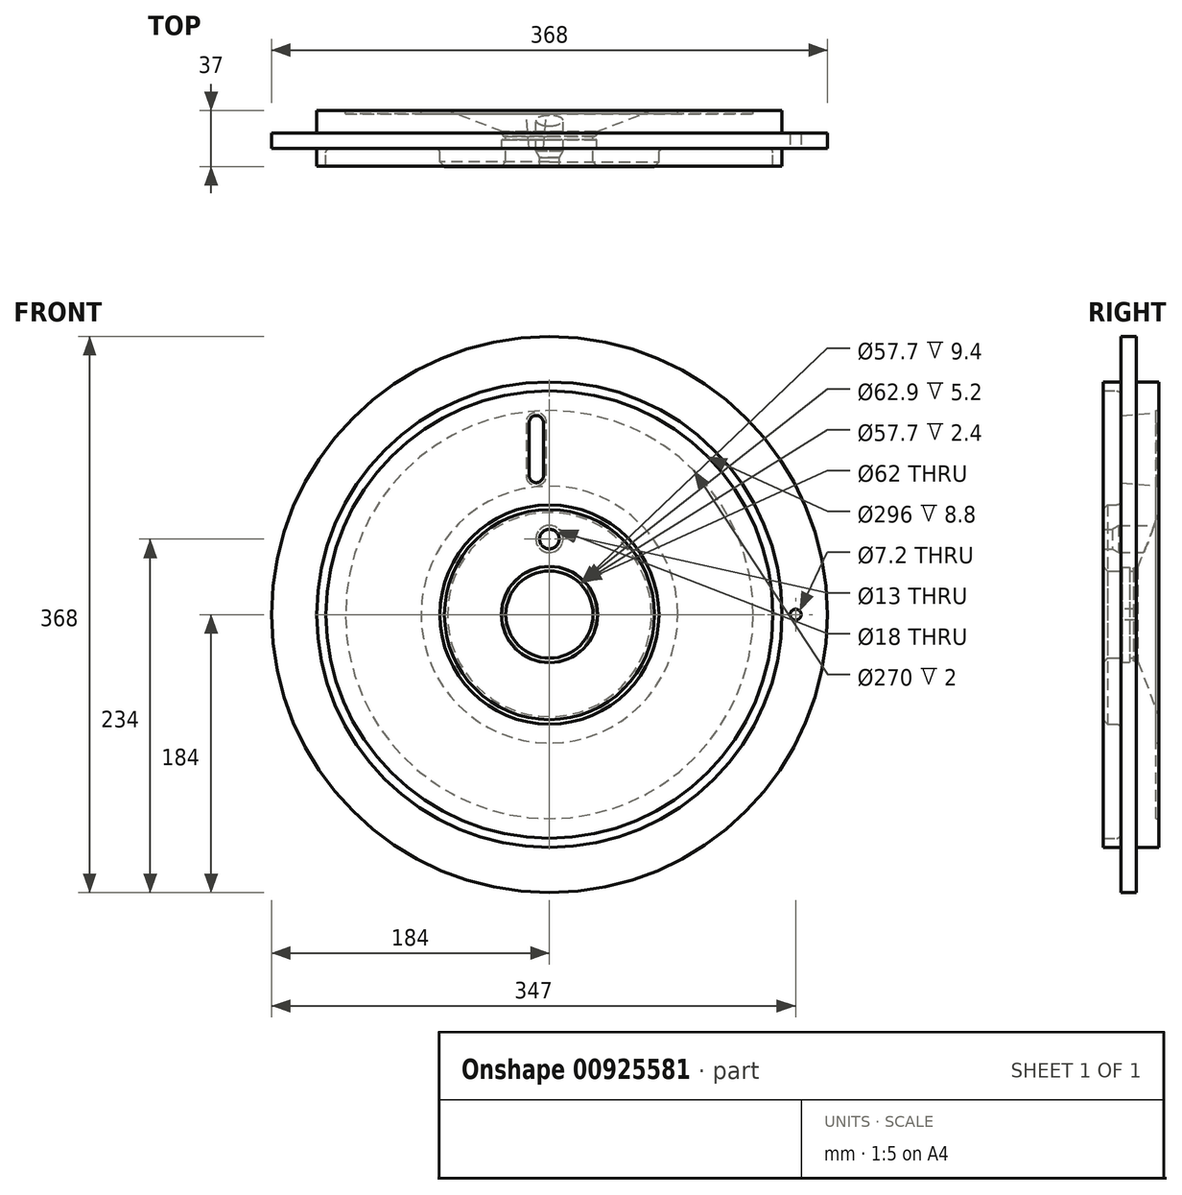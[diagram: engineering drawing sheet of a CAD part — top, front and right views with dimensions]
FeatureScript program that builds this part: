
annotation { "Feature Type Name" : "Feature", "Feature Type Description" : "" }
export const myFeature = defineFeature(function(context is Context, id is Id, definition is map)
    precondition{}
    {
        {
            var Q0;
            Q0=qCreatedBy(makeId("Top.planeOp"),FACE);
            var sketch = newSketch(context, id + "F0", { "sketchPlane" : qUnion([Q0])});
            skLineSegment(sketch, "E0", {"start": v(-72.5, 9) * mm, "end": v(-72.5, 0) * mm});
            skLineSegment(sketch, "E1", {"start": v(-72.5, 0) * mm, "end": v(-28.85, 0) * mm});
            skLineSegment(sketch, "E2", {"start": v(0, 47.35) * mm, "end": v(0, -31.33) * mm, "construction": true});
            skPoint(sketch, "E3.visualSharp", {"position": v(-72.5, 10) * mm});
            skLineSegment(sketch, "E4", {"start": v(-22.07, -0.9) * mm, "end": v(27.18, -0.9) * mm, "construction": true});
            skLineSegment(sketch, "E5", {"start": v(-154, 12) * mm, "end": v(-154, 0.2) * mm});
            skLineSegment(sketch, "E6", {"start": v(-154, 0.2) * mm, "end": v(-148, 0.2) * mm});
            skLineSegment(sketch, "E7", {"start": v(-148, 0.2) * mm, "end": v(-148, 9) * mm});
            skLineSegment(sketch, "E8", {"start": v(-28.85, 20) * mm, "end": v(-30, 20) * mm});
            skPoint(sketch, "E9.visualSharp", {"position": v(-35.7, 20) * mm});
            skLineSegment(sketch, "E10", {"start": v(-28.85, 20) * mm, "end": v(-28.85, 17.6) * mm});
            skLineSegment(sketch, "E11", {"start": v(-28.85, 17.6) * mm, "end": v(-31.45, 17.6) * mm});
            skLineSegment(sketch, "E12", {"start": v(-31.45, 17.6) * mm, "end": v(-31.45, 12.4) * mm});
            skLineSegment(sketch, "E13", {"start": v(-31.45, 12.4) * mm, "end": v(-28.85, 12.4) * mm});
            skLineSegment(sketch, "E14", {"start": v(-28.85, 12.4) * mm, "end": v(-28.85, 0) * mm});
            skLineSegment(sketch, "E15", {"start": v(-154, 12) * mm, "end": v(-184, 12) * mm});
            skLineSegment(sketch, "E16", {"start": v(-154, 37) * mm, "end": v(-67.5, 37) * mm});
            skPoint(sketch, "E17.visualSharp", {"position": v(-35, 23.4) * mm});
            skLineSegment(sketch, "E18", {"start": v(-145, 12) * mm, "end": v(-75.5, 12) * mm});
            skPoint(sketch, "E19.orphan", {"position": v(-148, 11.2) * mm});
            skPoint(sketch, "E20.visualSharp", {"position": v(-148, 12) * mm});
            skArc(sketch, "E20.filletArc", {"start": v(-145, 12) * mm, "mid": v(-147.12, 11.12) * mm, "end": v(-148, 9) * mm});
            skPoint(sketch, "E21.visualSharp", {"position": v(-72.5, 12) * mm});
            skArc(sketch, "E21.filletArc", {"start": v(-72.5, 9) * mm, "mid": v(-73.38, 11.12) * mm, "end": v(-75.5, 12) * mm});
            skLineSegment(sketch, "E22", {"start": v(-184, 12) * mm, "end": v(-184, 22) * mm});
            skLineSegment(sketch, "E23", {"start": v(-184, 22) * mm, "end": v(-154, 22) * mm});
            skLineSegment(sketch, "E24", {"start": v(-154, 22) * mm, "end": v(-154, 37) * mm});
            skLineSegment(sketch, "E25", {"start": v(-31, 23) * mm, "end": v(-67.5, 37) * mm});
            skLineSegment(sketch, "E26", {"start": v(-31, 23) * mm, "end": v(-31, 21) * mm});
            skPoint(sketch, "E27.visualSharp", {"position": v(-31, 20) * mm});
            skArc(sketch, "E27.filletArc", {"start": v(-31, 21) * mm, "mid": v(-30.7, 20.3) * mm, "end": v(-30, 20) * mm});
            skSolve(sketch);
        }
        {
            var Q0;
            Q0=makeQuery(id+"F0.imprint","IMPRINT",FACE,{"disambiguationData":[TD([[makeQuery(id+"F0.imprint","IMPRINT",EDGE,{"derivedFrom":sQuery(id+"F0.wireOp",EDGE,"E0")}),1.0]])]});
            var Q1;
            Q1=sQuery(id+"F0.wireOp",EDGE,"E2");
            revolve(context, id + "F1", {"surfaceOperationType" : NewSurfaceOperationType.NEW, "entities" : qUnion([Q0]), "axis" : qUnion([Q1]), "revolveType" : RevolveType.FULL});
        }
        {
            var Q0;
            Q0=qCreatedBy(makeId("Front.planeOp"),FACE);
            cPlane(context, id + "F2", {"entities" : qUnion([Q0]), "cplaneType" : CPlaneType.OFFSET, "offset" : 38 * mm, "oppositeDirection" : true, "width" : 150 * mm, "height" : 150 * mm});
        }
        {
            var Q0;
            Q0=qCreatedBy(makeId("Front.planeOp"),FACE);
            var sketch = newSketch(context, id + "F3", { "sketchPlane" : qUnion([Q0])});
            skCircle(sketch, "E28", {"center": v(163, 0) * mm, "radius": 3.6 * mm});
            skSolve(sketch);
        }
        {
            var Q0;
            Q0=qSketchRegion(id+"F3",true);
            extrude(context, id + "F4", {"entities" : qUnion([Q0]), "operationType" : NewBodyOperationType.REMOVE, "oppositeDirection" : true, "depth" : 50 * mm, "offsetDistance" : 25 * mm});
        }
        {
            var Q0;
            Q0=qCreatedBy(makeId("Right.planeOp"),FACE);
            var sketch = newSketch(context, id + "F5", { "sketchPlane" : qUnion([Q0])});
            skLineSegment(sketch, "E29", {"start": v(0, 50) * mm, "end": v(51.06, 50) * mm});
            skLineSegment(sketch, "E30", {"start": v(0, 56.5) * mm, "end": v(6, 56.5) * mm});
            skLineSegment(sketch, "E31", {"start": v(6, 56.5) * mm, "end": v(10.33, 59) * mm});
            skLineSegment(sketch, "E32", {"start": v(10.33, 59) * mm, "end": v(51.06, 59) * mm});
            skLineSegment(sketch, "E33", {"start": v(51.06, 59) * mm, "end": v(51.06, 50) * mm});
            skLineSegment(sketch, "E34", {"start": v(0, 50) * mm, "end": v(0, 56.5) * mm});
            skSolve(sketch);
        }
        {
            var Q0;
            Q0=qSketchRegion(id+"F5",true);
            var Q1;
            Q1=sQuery(id+"F5.wireOp",EDGE,"E29");
            revolve(context, id + "F6", {"operationType" : NewBodyOperationType.REMOVE, "surfaceOperationType" : NewSurfaceOperationType.NEW, "entities" : qUnion([Q0]), "axis" : qUnion([Q1]), "revolveType" : RevolveType.FULL, "oppositeDirection" : true});
        }
        {
            var Q0;
            Q0=makeQuery(id+"F1.opRevolve","SWEPT_EDGE",EDGE,{"disambiguationData":[OSD([sQuery(id+"F0.wireOp",EDGE,"GnCOIqdh-ukie-yiku-SOtR-T2upxGWuMmtm"),sQuery(id+"F0.wireOp",EDGE,"E1")])]});
            chamfer(context, id + "F7", {"entities" : qUnion([Q0]), "width" : 3 * mm, "tangentPropagation" : true});
        }
        {
            var Q0;
            Q0=qCreatedBy(id+"F2.planeOp",FACE);
            var sketch = newSketch(context, id + "F8", { "sketchPlane" : qUnion([Q0])});
            skCircle(sketch, "E35", {"center": v(0, 0) * mm, "radius": 85 * mm});
            skCircle(sketch, "E36", {"center": v(0, 0) * mm, "radius": 135 * mm});
            skSolve(sketch);
        }
        {
            var Q0;
            Q0=qSketchRegion(id+"F8",true);
            var Q1;
            Q1=makeQuery(id+"F1.opRevolve","SWEPT_FACE",FACE,{"disambiguationData":[OSD([sQuery(id+"F0.wireOp",EDGE,"E16")])]});
            extrude(context, id + "F9", {"entities" : qUnion([Q0]), "operationType" : NewBodyOperationType.REMOVE, "endBound" : BoundingType.UP_TO_SURFACE, "depth" : 25 * mm, "endBoundEntityFace" : qUnion([Q1]), "hasOffset" : true, "offsetDistance" : 2 * mm, "offsetOppositeDirection" : true});
        }
        {
            var Q0;
            Q0=qCreatedBy(id+"F2.planeOp",FACE);
            var sketch = newSketch(context, id + "F10", { "sketchPlane" : qUnion([Q0])});
            skLineSegment(sketch, "E37", {"start": v(0, 0) * mm, "end": v(0, 136.44) * mm, "construction": true});
            skLineSegment(sketch, "E38", {"start": v(-8.7, 134) * mm, "end": v(-8.7, 134) * mm});
            skLineSegment(sketch, "E39", {"start": v(-15.7, 127) * mm, "end": v(-15.7, 92) * mm});
            skLineSegment(sketch, "E40", {"start": v(-8.7, 85) * mm, "end": v(-8.7, 85) * mm});
            skLineSegment(sketch, "E41", {"start": v(-1.7, 92) * mm, "end": v(-1.7, 127) * mm});
            skPoint(sketch, "E42.visualSharp", {"position": v(-15.7, 134) * mm});
            skArc(sketch, "E42.filletArc", {"start": v(-8.7, 134) * mm, "mid": v(-13.65, 131.95) * mm, "end": v(-15.7, 127) * mm});
            skPoint(sketch, "E43.visualSharp", {"position": v(-1.7, 134) * mm});
            skArc(sketch, "E43.filletArc", {"start": v(-1.7, 127) * mm, "mid": v(-3.75, 131.95) * mm, "end": v(-8.7, 134) * mm});
            skPoint(sketch, "E44.visualSharp", {"position": v(-1.7, 85) * mm});
            skArc(sketch, "E44.filletArc", {"start": v(-8.7, 85) * mm, "mid": v(-3.75, 87.05) * mm, "end": v(-1.7, 92) * mm});
            skPoint(sketch, "E45.visualSharp", {"position": v(-15.7, 85) * mm});
            skArc(sketch, "E45.filletArc", {"start": v(-15.7, 92) * mm, "mid": v(-13.65, 87.05) * mm, "end": v(-8.7, 85) * mm});
            skSolve(sketch);
        }
        {
            var Q0;
            Q0=qSketchRegion(id+"F10",true);
            extrude(context, id + "F11", {"entities" : qUnion([Q0]), "operationType" : NewBodyOperationType.REMOVE, "depth" : 50 * mm, "offsetDistance" : 25 * mm, "hasDraft" : true, "draftAngle" : 5 * degree, "draftPullDirection" : true});
        }
    });
